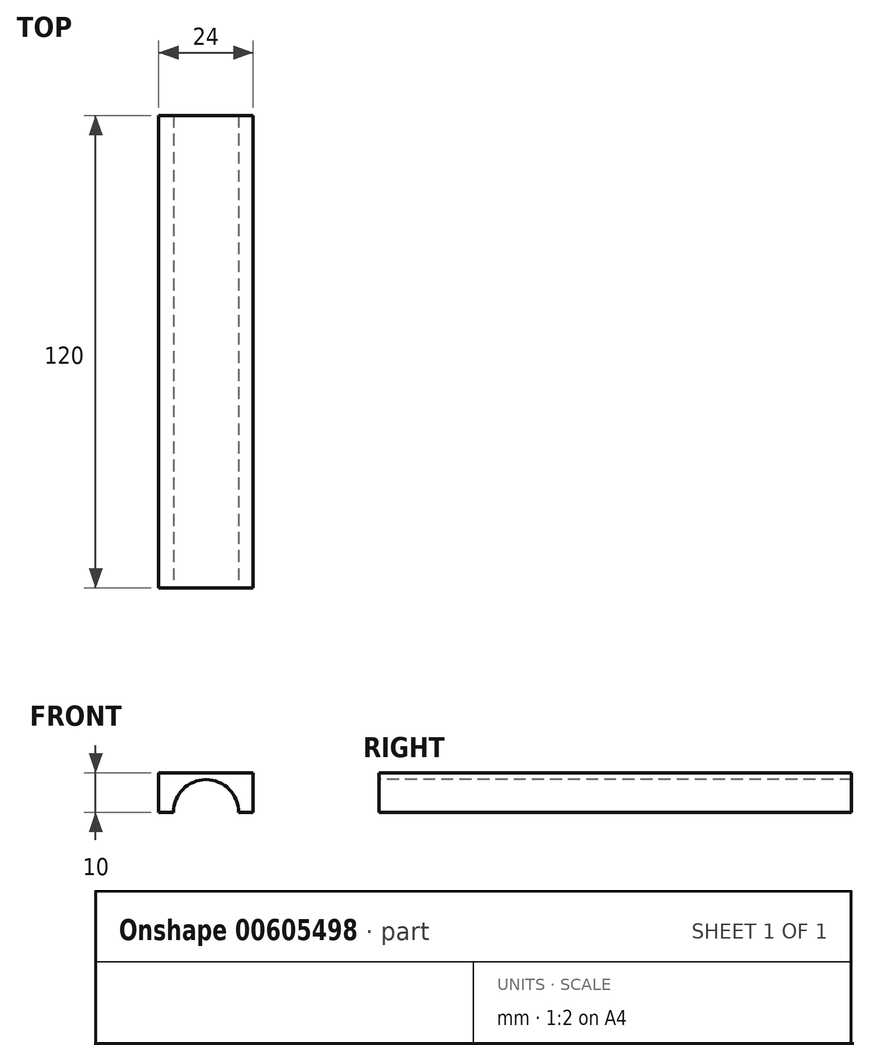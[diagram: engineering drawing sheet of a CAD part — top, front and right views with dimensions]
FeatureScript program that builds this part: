
annotation { "Feature Type Name" : "Feature", "Feature Type Description" : "" }
export const myFeature = defineFeature(function(context is Context, id is Id, definition is map)
    precondition{}
    {
        {
            var Q0;
            Q0=qCreatedBy(makeId("Front.planeOp"),FACE);
            var sketch = newSketch(context, id + "F0", { "sketchPlane" : qUnion([Q0])});
            skLineSegment(sketch, "E0.bottom", {"start": v(5.01, 0) * mm, "end": v(-18.99, 0) * mm});
            skLineSegment(sketch, "E0.top", {"start": v(5.01, 24) * mm, "end": v(-18.99, 24) * mm});
            skLineSegment(sketch, "E0.left", {"start": v(5.01, 0) * mm, "end": v(5.01, 24) * mm});
            skLineSegment(sketch, "E0.right", {"start": v(-18.99, 0) * mm, "end": v(-18.99, 24) * mm});
            skSolve(sketch);
        }
        {
            var Q0;
            Q0=makeQuery(id+"F0.imprint","IMPRINT",FACE,{"disambiguationData":[TD([[makeQuery(id+"F0.imprint","IMPRINT",EDGE,{"derivedFrom":sQuery(id+"F0.wireOp",EDGE,"E0.bottom")}),-1.0]])]});
            extrude(context, id + "F1", {"entities" : qUnion([Q0]), "depth" : 120 * mm, "offsetDistance" : 25 * mm});
        }
        {
            var Q0;
            Q0=makeQuery(id+"F1.opExtrude","CAP_FACE",FACE,{"disambiguationData":[OSD([sQuery(id+"F0.wireOp",EDGE,"E0.bottom"),sQuery(id+"F0.wireOp",EDGE,"E0.top"),sQuery(id+"F0.wireOp",EDGE,"E0.left"),sQuery(id+"F0.wireOp",EDGE,"E0.right")])],"isStart":false});
            var sketch = newSketch(context, id + "F2", { "sketchPlane" : qUnion([Q0])});
            skCircle(sketch, "E1", {"center": v(-6.99, 0) * mm, "radius": 8.3 * mm});
            skSolve(sketch);
        }
        {
            var Q0;
            Q0 = qSketchRegion(id + "F2", true);
            extrude(context, id + "F3", {"entities" : qUnion([Q0]), "operationType" : NewBodyOperationType.REMOVE, "oppositeDirection" : true, "depth" : 250 * mm, "offsetDistance" : 25 * mm});
        }
        {
            var Q0;
            Q0=makeQuery(id+"F1.opExtrude","CAP_FACE",FACE,{"disambiguationData":[OSD([sQuery(id+"F0.wireOp",EDGE,"E0.bottom"),sQuery(id+"F0.wireOp",EDGE,"E0.top"),sQuery(id+"F0.wireOp",EDGE,"E0.left"),sQuery(id+"F0.wireOp",EDGE,"E0.right")])],"isStart":false});
            var sketch = newSketch(context, id + "F4", { "sketchPlane" : qUnion([Q0])});
            skLineSegment(sketch, "E2.bottom", {"start": v(-21.39, 24) * mm, "end": v(7.38, 24) * mm});
            skLineSegment(sketch, "E2.top", {"start": v(-21.39, 10) * mm, "end": v(7.38, 10) * mm});
            skLineSegment(sketch, "E2.left", {"start": v(-21.39, 24) * mm, "end": v(-21.39, 10) * mm});
            skLineSegment(sketch, "E2.right", {"start": v(7.38, 24) * mm, "end": v(7.38, 10) * mm});
            skSolve(sketch);
        }
        {
            var Q0;
            Q0 = qSketchRegion(id + "F4", true);
            var Q1;
            {var subQ3=sQuery(id+"F4.wireOp",EDGE,"E2.right");Q1=makeQuery(id+"F4.imprint","IMPRINT",FACE,{"disambiguationData":[TD([[makeQuery(id+"F4.imprint","IMPRINT",EDGE,{"derivedFrom":subQ3}),-1.0]])]});}
            var Q2;
            {var subQ3=sQuery(id+"F4.wireOp",EDGE,"E2.left");Q2=makeQuery(id+"F4.imprint","IMPRINT",FACE,{"disambiguationData":[TD([[makeQuery(id+"F4.imprint","IMPRINT",EDGE,{"derivedFrom":subQ3}),1.0]])]});}
            var Q3;
            {var subQ0=sQuery(id+"F4.wireOp",EDGE,"E2.bottom");var subQ1=makeQuery(id+"F1.opExtrude","CAP_EDGE",EDGE,{"disambiguationData":[OSD([sQuery(id+"F0.wireOp",EDGE,"E0.left")])],"isStart":false});var subQ2=makeQuery(id+"F4.imprint","INTERSECT",VERTEX,{"derivedFrom":[subQ1,subQ0]});var subQ3=makeQuery(id+"F1.opExtrude","CAP_EDGE",EDGE,{"disambiguationData":[OSD([sQuery(id+"F0.wireOp",EDGE,"E0.right")])],"isStart":false});var subQ4=makeQuery(id+"F4.imprint","INTERSECT",VERTEX,{"derivedFrom":[subQ3,subQ0]});Q3=makeQuery(id+"F4.imprint","IMPRINT",FACE,{"disambiguationData":[TD([[makeQuery(id+"F4.imprint","IMPRINT",EDGE,{"disambiguationData":[TD([[subQ2,-1.0],[subQ4,1.0]])],"derivedFrom":subQ0}),1.0]])]});}
            extrude(context, id + "F5", {"entities" : qUnion([Q0, Q1, Q2, Q3]), "operationType" : NewBodyOperationType.REMOVE, "oppositeDirection" : true, "depth" : 250 * mm, "offsetDistance" : 25 * mm});
        }
    });
